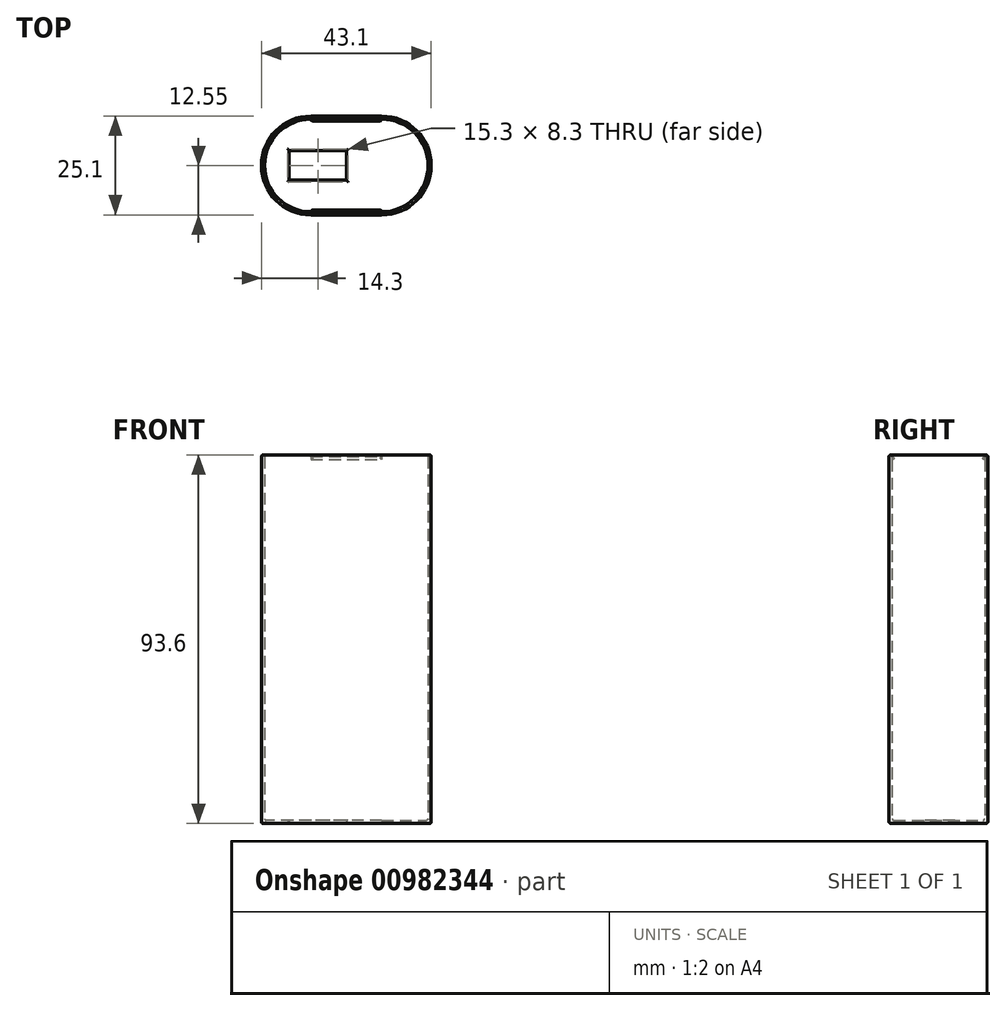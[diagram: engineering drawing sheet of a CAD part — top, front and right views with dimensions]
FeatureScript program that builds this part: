
annotation { "Feature Type Name" : "Feature", "Feature Type Description" : "" }
export const myFeature = defineFeature(function(context is Context, id is Id, definition is map)
    precondition{}
    {
        {
            var Q0;
            Q0=qCreatedBy(makeId("Top.planeOp"),FACE);
            var sketch = newSketch(context, id + "F0", { "sketchPlane" : qUnion([Q0])});
            skLineSegment(sketch, "E0.bottom", {"start": v(-9, 11.75) * mm, "end": v(9, 11.75) * mm});
            skLineSegment(sketch, "E0.top", {"start": v(-9, -11.75) * mm, "end": v(9, -11.75) * mm});
            skPoint(sketch, "E0.middle", {"position": v(0, 0) * mm});
            skArc(sketch, "E1", {"start": v(-9, 11.75) * mm, "mid": v(-20.75, 0) * mm, "end": v(-9, -11.75) * mm});
            skArc(sketch, "E2", {"start": v(9, -11.75) * mm, "mid": v(20.75, 0) * mm, "end": v(9, 11.75) * mm});
            skPoint(sketch, "E3.orphan", {"position": v(-20.75, -11.75) * mm});
            skPoint(sketch, "E4.orphan", {"position": v(-20.75, 11.75) * mm});
            skPoint(sketch, "E5.orphan", {"position": v(20.75, 11.75) * mm});
            skPoint(sketch, "E6.orphan", {"position": v(20.75, -11.75) * mm});
            skLineSegment(sketch, "E7.0", {"start": v(-9, 12.55) * mm, "end": v(9, 12.55) * mm});
            skArc(sketch, "E7.1", {"start": v(-9, 12.55) * mm, "mid": v(-21.55, 0) * mm, "end": v(-9, -12.55) * mm});
            skLineSegment(sketch, "E7.2", {"start": v(-9, -12.55) * mm, "end": v(9, -12.55) * mm});
            skArc(sketch, "E7.3", {"start": v(9, -12.55) * mm, "mid": v(21.55, 0) * mm, "end": v(9, 12.55) * mm});
            skLineSegment(sketch, "E8.bottom", {"start": v(0, 3.75) * mm, "end": v(-14.5, 3.75) * mm});
            skLineSegment(sketch, "E8.top", {"start": v(0, -3.75) * mm, "end": v(-14.5, -3.75) * mm});
            skLineSegment(sketch, "E8.left", {"start": v(0, 3.75) * mm, "end": v(0, -3.75) * mm});
            skLineSegment(sketch, "E8.right", {"start": v(-14.5, 3.75) * mm, "end": v(-14.5, -3.75) * mm});
            skPoint(sketch, "E8.middle", {"position": v(-7.25, 0) * mm});
            skSolve(sketch);
        }
        {
            var Q0;
            Q0=makeQuery(id+"F0.imprint","IMPRINT",FACE,{"disambiguationData":[TD([[makeQuery(id+"F0.imprint","IMPRINT",EDGE,{"derivedFrom":sQuery(id+"F0.wireOp",EDGE,"E0.bottom")}),1.0]])]});
            var Q1;
            Q1=makeQuery(id+"F0.imprint","IMPRINT",FACE,{"disambiguationData":[TD([[makeQuery(id+"F0.imprint","IMPRINT",EDGE,{"derivedFrom":sQuery(id+"F0.wireOp",EDGE,"E0.bottom")}),-1.0]])]});
            extrude(context, id + "F1", {"entities" : qUnion([Q0, Q1]), "depth" : .8 * mm, "offsetDistance" : 25 * mm});
        }
        {
            var Q0;
            Q0=makeQuery(id+"F0.imprint","IMPRINT",FACE,{"disambiguationData":[TD([[makeQuery(id+"F0.imprint","IMPRINT",EDGE,{"derivedFrom":sQuery(id+"F0.wireOp",EDGE,"E0.bottom")}),1.0]])]});
            extrude(context, id + "F2", {"entities" : qUnion([Q0]), "operationType" : NewBodyOperationType.ADD, "depth" : 93.6 * mm, "offsetDistance" : 25 * mm});
        }
        {
            var Q0;
            Q0=makeQuery(id+"F2.opExtrude","CAP_EDGE",EDGE,{"disambiguationData":[OSD([sQuery(id+"F0.wireOp",EDGE,"E7.2")])],"isStart":false});
            var Q1;
            Q1=makeQuery(id+"F2.opExtrude","CAP_EDGE",EDGE,{"disambiguationData":[OSD([sQuery(id+"F0.wireOp",EDGE,"E0.top")])],"isStart":false});
            var Q2;
            Q2=makeQuery(id+"F1.opExtrude","CAP_EDGE",EDGE,{"disambiguationData":[OSD([sQuery(id+"F0.wireOp",EDGE,"E7.2")])],"isStart":true});
            var Q3;
            Q3=makeQuery(id+"F1.opExtrude","CAP_EDGE",EDGE,{"disambiguationData":[OSD([sQuery(id+"F0.wireOp",EDGE,"OiciUjBS-RVEL-95kf-2NiY-lDI2oKAl4VR3")])],"isStart":false});
            var Q4;
            Q4=makeQuery(id+"F1.opExtrude","CAP_EDGE",EDGE,{"disambiguationData":[OSD([sQuery(id+"F0.wireOp",EDGE,"OiciUjBS-RVEL-95kf-2NiY-lDI2oKAl4VR3")])],"isStart":true});
            var Q5;
            Q5=makeQuery(id+"F1.opExtrude","CAP_EDGE",EDGE,{"disambiguationData":[OSD([sQuery(id+"F0.wireOp",EDGE,"K6H06pX5-4ONF-FUig-rYAk-WZB2ePW42RMd")])],"isStart":true});
            var Q6;
            Q6=makeQuery(id+"F1.opExtrude","CAP_EDGE",EDGE,{"disambiguationData":[OSD([sQuery(id+"F0.wireOp",EDGE,"K6H06pX5-4ONF-FUig-rYAk-WZB2ePW42RMd")])],"isStart":false});
            var Q7;
            Q7=makeQuery(id+"F1.opExtrude","CAP_EDGE",EDGE,{"disambiguationData":[OSD([sQuery(id+"F0.wireOp",EDGE,"E8.bottom")])],"isStart":true});
            var Q8;
            Q8=makeQuery(id+"F1.opExtrude","CAP_EDGE",EDGE,{"disambiguationData":[OSD([sQuery(id+"F0.wireOp",EDGE,"E8.bottom")])],"isStart":false});
            var Q9;
            Q9=makeQuery(id+"F1.opExtrude","CAP_EDGE",EDGE,{"disambiguationData":[OSD([sQuery(id+"F0.wireOp",EDGE,"E8.right")])],"isStart":true});
            var Q10;
            Q10=makeQuery(id+"F1.opExtrude","CAP_EDGE",EDGE,{"disambiguationData":[OSD([sQuery(id+"F0.wireOp",EDGE,"E8.right")])],"isStart":false});
            var Q11;
            Q11=makeQuery(id+"F1.opExtrude","CAP_EDGE",EDGE,{"disambiguationData":[OSD([sQuery(id+"F0.wireOp",EDGE,"E8.top")])],"isStart":true});
            var Q12;
            Q12=makeQuery(id+"F1.opExtrude","CAP_EDGE",EDGE,{"disambiguationData":[OSD([sQuery(id+"F0.wireOp",EDGE,"E8.top")])],"isStart":false});
            var Q13;
            Q13=makeQuery(id+"F1.opExtrude","CAP_EDGE",EDGE,{"disambiguationData":[OSD([sQuery(id+"F0.wireOp",EDGE,"E8.left")])],"isStart":true});
            var Q14;
            Q14=makeQuery(id+"F1.opExtrude","CAP_EDGE",EDGE,{"disambiguationData":[OSD([sQuery(id+"F0.wireOp",EDGE,"E8.left")])],"isStart":false});
            fillet(context, id + "F3", {"entities" : qUnion([Q0, Q1, Q2, Q3, Q4, Q5, Q6, Q7, Q8, Q9, Q10, Q11, Q12, Q13, Q14]), "radius" : .4 * mm, "tangentPropagation" : true, "allowEdgeOverflow" : false});
        }
        {
            var Q0;
            Q0=makeQuery(id+"F2.boolean.opBoolean","INTERSECT",EDGE,{"derivedFrom":[makeQuery(id+"F1.opExtrude","CAP_FACE",FACE,{"disambiguationData":[OSD([sQuery(id+"F0.wireOp",EDGE,"E7.0"),sQuery(id+"F0.wireOp",EDGE,"E7.1"),sQuery(id+"F0.wireOp",EDGE,"E7.2"),sQuery(id+"F0.wireOp",EDGE,"E7.3")])],"isStart":false}),makeQuery(id+"F2.opExtrude","SWEPT_FACE",FACE,{"disambiguationData":[OSD([sQuery(id+"F0.wireOp",EDGE,"E0.bottom")])]})]});
            fillet(context, id + "F4", {"entities" : qUnion([Q0]), "radius" : .4 * mm, "tangentPropagation" : true, "allowEdgeOverflow" : false});
        }
        {
            var Q0;
            Q0=makeQuery(id+"F2.opExtrude","SWEPT_FACE",FACE,{"disambiguationData":[OSD([sQuery(id+"F0.wireOp",EDGE,"E0.bottom")])]});
            var sketch = newSketch(context, id + "F5", { "sketchPlane" : qUnion([Q0])});
            skLineSegment(sketch, "E9.bottom", {"start": v(-9, 93.2) * mm, "end": v(9, 93.2) * mm});
            skLineSegment(sketch, "E9.top", {"start": v(-9, 92.4) * mm, "end": v(9, 92.4) * mm});
            skLineSegment(sketch, "E9.left", {"start": v(-9, 93.2) * mm, "end": v(-9, 92.4) * mm});
            skLineSegment(sketch, "E9.right", {"start": v(9, 93.2) * mm, "end": v(9, 92.4) * mm});
            skSolve(sketch);
        }
        {
            var Q0;
            Q0=makeQuery(id+"F2.opExtrude","SWEPT_FACE",FACE,{"disambiguationData":[OSD([sQuery(id+"F0.wireOp",EDGE,"E0.top")])]});
            var sketch = newSketch(context, id + "F6", { "sketchPlane" : qUnion([Q0])});
            skLineSegment(sketch, "E10.bottom", {"start": v(-9, 93.2) * mm, "end": v(9, 93.2) * mm});
            skLineSegment(sketch, "E10.top", {"start": v(-9, 92.4) * mm, "end": v(9, 92.4) * mm});
            skLineSegment(sketch, "E10.left", {"start": v(-9, 93.2) * mm, "end": v(-9, 92.4) * mm});
            skLineSegment(sketch, "E10.right", {"start": v(9, 93.2) * mm, "end": v(9, 92.4) * mm});
            skSolve(sketch);
        }
        {
            var Q0;
            Q0=makeQuery(id+"F5.imprint","IMPRINT",FACE,{"disambiguationData":[TD([[makeQuery(id+"F5.imprint","IMPRINT",EDGE,{"derivedFrom":sQuery(id+"F5.wireOp",EDGE,"E9.bottom")}),1.0]])]});
            var Q1;
            Q1=makeQuery(id+"F6.imprint","IMPRINT",FACE,{"disambiguationData":[TD([[makeQuery(id+"F6.imprint","IMPRINT",EDGE,{"derivedFrom":sQuery(id+"F6.wireOp",EDGE,"E10.bottom")}),1.0]])]});
            extrude(context, id + "F7", {"entities" : qUnion([Q0, Q1]), "operationType" : NewBodyOperationType.ADD, "endBound" : BoundingType.SYMMETRIC, "depth" : .8 * mm, "offsetDistance" : 25 * mm});
        }
        {
            var Q0;
            Q0=makeQuery(id+"F7.opExtrude","CAP_EDGE",EDGE,{"disambiguationData":[OSD([sQuery(id+"F5.wireOp",EDGE,"E9.bottom")])],"isStart":false});
            var Q1;
            Q1=makeQuery(id+"F7.opExtrude","CAP_EDGE",EDGE,{"disambiguationData":[OSD([sQuery(id+"F5.wireOp",EDGE,"E9.top")])],"isStart":false});
            var Q2;
            Q2=makeQuery(id+"F7.opExtrude","CAP_EDGE",EDGE,{"disambiguationData":[OSD([sQuery(id+"F5.wireOp",EDGE,"E9.left")])],"isStart":false});
            var Q3;
            Q3=makeQuery(id+"F7.opExtrude","CAP_EDGE",EDGE,{"disambiguationData":[OSD([sQuery(id+"F5.wireOp",EDGE,"E9.right")])],"isStart":false});
            var Q4;
            Q4=makeQuery(id+"F7.opExtrude","CAP_EDGE",EDGE,{"disambiguationData":[OSD([sQuery(id+"F6.wireOp",EDGE,"E10.bottom")])],"isStart":true});
            var Q5;
            Q5=makeQuery(id+"F7.opExtrude","CAP_EDGE",EDGE,{"disambiguationData":[OSD([sQuery(id+"F6.wireOp",EDGE,"E10.top")])],"isStart":true});
            var Q6;
            Q6=makeQuery(id+"F7.opExtrude","CAP_EDGE",EDGE,{"disambiguationData":[OSD([sQuery(id+"F6.wireOp",EDGE,"E10.left")])],"isStart":true});
            var Q7;
            Q7=makeQuery(id+"F7.opExtrude","CAP_EDGE",EDGE,{"disambiguationData":[OSD([sQuery(id+"F6.wireOp",EDGE,"E10.right")])],"isStart":true});
            fillet(context, id + "F8", {"entities" : qUnion([Q0, Q1, Q2, Q3, Q4, Q5, Q6, Q7]), "radius" : .4 * mm, "tangentPropagation" : true, "allowEdgeOverflow" : false});
        }
    });
